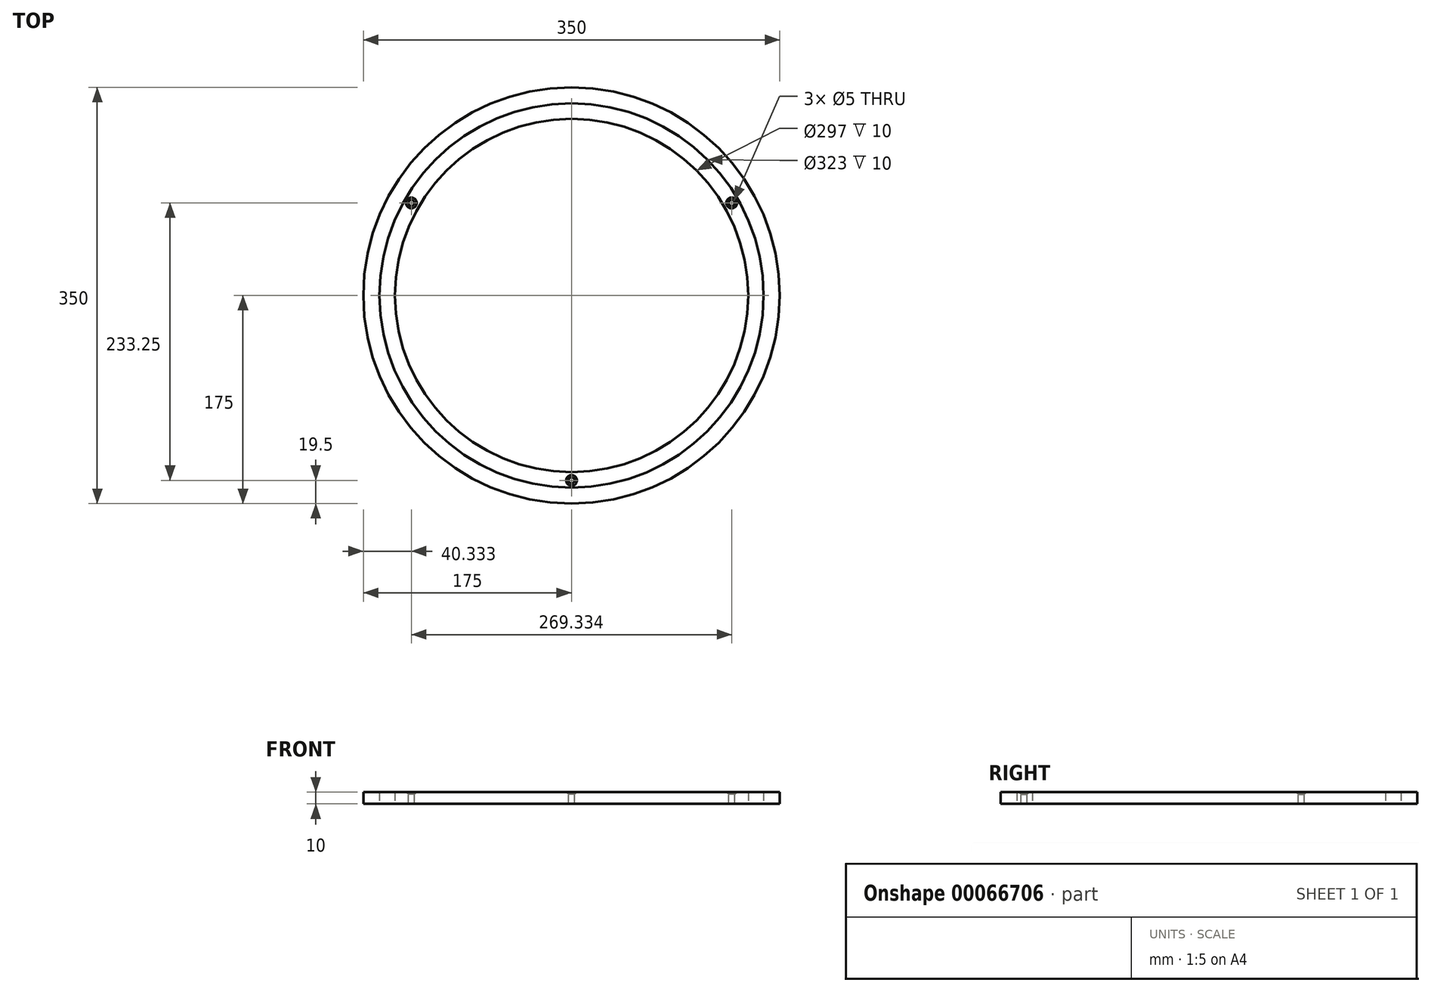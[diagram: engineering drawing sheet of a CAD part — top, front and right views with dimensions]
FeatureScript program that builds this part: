
annotation { "Feature Type Name" : "Feature", "Feature Type Description" : "" }
export const myFeature = defineFeature(function(context is Context, id is Id, definition is map)
    precondition{}
    {
        {
            var Q0;
            Q0=qCreatedBy(makeId("Top.planeOp"),FACE);
            var sketch = newSketch(context, id + "F0", { "sketchPlane" : qUnion([Q0])});
            skCircle(sketch, "E0", {"center": v(0, 0) * mm, "radius": 161.5 * mm});
            skCircle(sketch, "E1", {"center": v(0, 0) * mm, "radius": 148.5 * mm});
            skCircle(sketch, "E2", {"center": v(0, 0) * mm, "radius": 175 * mm});
            skSolve(sketch);
        }
        {
            var Q0;
            Q0=makeQuery(id+"F0.imprint","IMPRINT",FACE,{"disambiguationData":[TD([[makeQuery(id+"F0.imprint","IMPRINT",EDGE,{"derivedFrom":sQuery(id+"F0.wireOp",EDGE,"E0")}),-1.0]])]});
            extrude(context, id + "F1", {"entities" : qUnion([Q0]), "depth" : 5 * mm, "hasSecondDirection" : true, "secondDirectionOppositeDirection" : true, "secondDirectionDepth" : 5 * mm});
        }
        {
            var Q0;
            Q0=makeQuery(id+"F0.imprint","IMPRINT",FACE,{"disambiguationData":[TD([[makeQuery(id+"F0.imprint","IMPRINT",EDGE,{"derivedFrom":sQuery(id+"F0.wireOp",EDGE,"E0")}),1.0]])]});
            var Q1;
            Q1=makeQuery(id+"F1.opExtrude","CAP_FACE",FACE,{"disambiguationData":[OSD([sQuery(id+"F0.wireOp",EDGE,"E0"),sQuery(id+"F0.wireOp",EDGE,"E2")])],"isStart":false});
            var Q2;
            Q2=makeQuery(id+"F1.opExtrude","CAP_FACE",FACE,{"disambiguationData":[OSD([sQuery(id+"F0.wireOp",EDGE,"E0"),sQuery(id+"F0.wireOp",EDGE,"E2")])],"isStart":true});
            extrude(context, id + "F2", {"entities" : qUnion([Q0]), "endBound" : BoundingType.UP_TO_SURFACE, "endBoundEntityFace" : qUnion([Q1]), "depth" : 25.4 * mm, "hasSecondDirection" : true, "secondDirectionBound" : SecondDirectionBoundingType.UP_TO_SURFACE, "secondDirectionOppositeDirection" : true, "secondDirectionBoundEntityFace" : qUnion([Q2]), "secondDirectionDepth" : 25.4 * mm});
        }
        {
            var Q0;
            Q0=makeQuery(id+"F2.opExtrude","CAP_FACE",FACE,{"disambiguationData":[OSD([sQuery(id+"F0.wireOp",EDGE,"E0"),sQuery(id+"F0.wireOp",EDGE,"E1")])],"isStart":false});
            var sketch = newSketch(context, id + "F3", { "sketchPlane" : qUnion([Q0])});
            skCircle(sketch, "E3.cCircle", {"center": v(0, 0) * mm, "radius": 155.5 * mm, "construction": true});
            skLineSegment(sketch, "E3.0", {"start": v(0, -155.5) * mm, "end": v(-134.67, -77.75) * mm, "construction": true});
            skLineSegment(sketch, "E3.1", {"start": v(-134.67, -77.75) * mm, "end": v(-134.67, 77.75) * mm, "construction": true});
            skLineSegment(sketch, "E3.2", {"start": v(-134.67, 77.75) * mm, "end": v(0, 155.5) * mm, "construction": true});
            skLineSegment(sketch, "E3.3", {"start": v(0, 155.5) * mm, "end": v(134.67, 77.75) * mm, "construction": true});
            skLineSegment(sketch, "E3.4", {"start": v(134.67, 77.75) * mm, "end": v(134.67, -77.75) * mm, "construction": true});
            skLineSegment(sketch, "E3.5", {"start": v(134.67, -77.75) * mm, "end": v(0, -155.5) * mm, "construction": true});
            skPoint(sketch, "E4", {"position": v(-134.67, 77.75) * mm});
            skPoint(sketch, "E5", {"position": v(0, -155.5) * mm});
            skPoint(sketch, "E6", {"position": v(134.67, 77.75) * mm});
            skSolve(sketch);
        }
        {
            var Q0;
            Q0=sQuery(id+"F3.wireOp",VERTEX,"E4");
            var Q1;
            Q1=sQuery(id+"F3.wireOp",VERTEX,"E6");
            var Q2;
            Q2=sQuery(id+"F3.wireOp",VERTEX,"E5");
            var Q3;
            Q3=makeQuery(id+"F2.opExtrude","SWEPT_BODY",BODY,{"disambiguationData":[OSD([sQuery(id+"F0.wireOp",EDGE,"E0"),sQuery(id+"F0.wireOp",EDGE,"E1")])]});
            hole(context, id + "F4", {"style" : HoleStyle.C_SINK, "holeDiameter" : 5 * mm, "cSinkDiameter" : 9 * mm, "endStyle" : HoleEndStyle.THROUGH, "locations" : qUnion([Q0, Q1, Q2]), "scope" : qUnion([Q3]), "cSinkAngle" : 90 * degree});
        }
    });
